# Revit family: MP15
name_source: partatom
category: Planting
revit_build: Autodesk Revit LT 2017 (Build: 20160225_1515(x64)
units: mm (PartAtom-declared; Revit-internal decimal feet)

## family parameters
Always vertical = No
Cut with Voids When Loaded = No
Render Appearance Source = Family Geometry
Shared = No
Work Plane-Based = Yes

## types (1)
- NBS Standard Parameters
    BIMObjectName = metpro_metprolibrary_channelcablesupports_channelbracket
    Default Elevation = 1219 mm
    Description = MP15  90 degree Tee Bracket
    DurationUnit = year
    Finish = Hot Dipped Galvanised
    Height = 0 mm  [stored 0 ft]
    Keynote = Compliant to LU Standard 1-085
    ManufacturerName = Metpro Ltd
    ManufacturerURL = www.metpro.co.uk
    Material = Steel
    ModelReference = MP15
    NBSDescription = Channel Cable Supports
    NBSReference = 90-55-10/305
    NominalHeight = 45 mm  [stored 0.147638 ft]
    NominalLength = 138 mm  [stored 0.452756 ft]
    NominalWidth = 46 mm  [stored 0.150919 ft]
    ProductInformation = www.metpro.co.uk/pdf/mp15.pdf
    Shape = Tee
    Size = 90 Degree
    Uniclass2 = Pr_65_70_11_19
    Version = 1
    WarrantyDurationUnit = 1 year
    Weight = 0.32Kg

note: [stored X ft] marks values corroborated as IEEE doubles in the binary element streams (Revit-internal decimal feet)

## geometry (parser evidence)
native form markers: Sweep x2
no freeform markers — native parametric forms only
